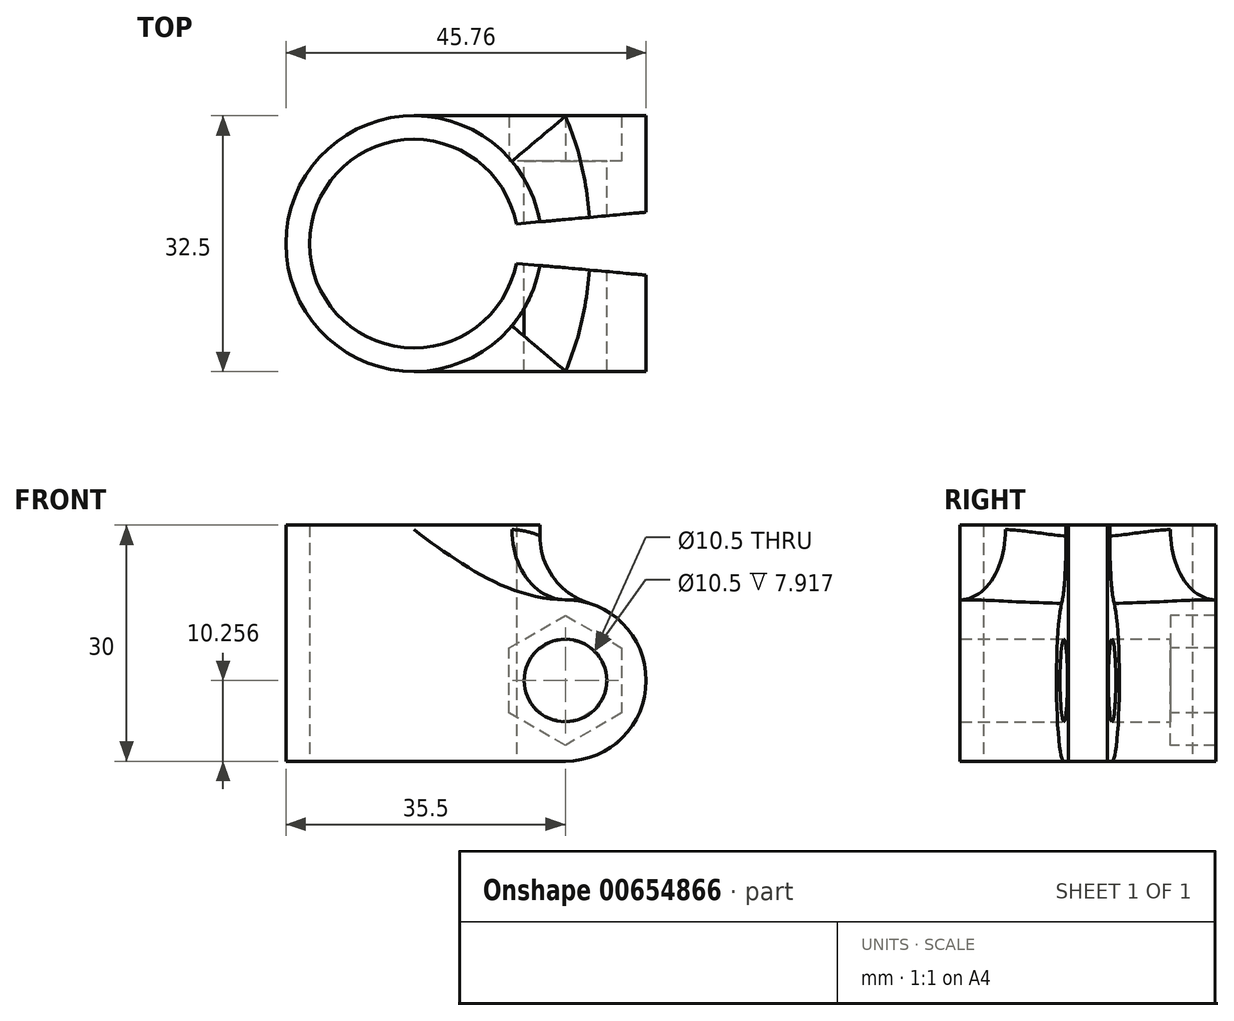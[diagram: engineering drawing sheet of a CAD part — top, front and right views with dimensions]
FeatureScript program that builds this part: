
annotation { "Feature Type Name" : "Feature", "Feature Type Description" : "" }
export const myFeature = defineFeature(function(context is Context, id is Id, definition is map)
    precondition{}
    {
        {
            var Q0;
            Q0=qCreatedBy(makeId("Top.planeOp"),FACE);
            var sketch = newSketch(context, id + "F0", { "sketchPlane" : qUnion([Q0])});
            skCircle(sketch, "E0", {"center": v(0, 0) * mm, "radius": 13.25 * mm});
            skCircle(sketch, "E1.0", {"center": v(0, 0) * mm, "radius": 16.25 * mm});
            skPoint(sketch, "E2", {"position": v(16.25, 0) * mm});
            skLineSegment(sketch, "E3.bottom", {"start": v(13.01, 2.5) * mm, "end": v(50, 2.5) * mm});
            skLineSegment(sketch, "E3.top", {"start": v(13.01, -2.5) * mm, "end": v(50, -2.5) * mm});
            skLineSegment(sketch, "E3.right", {"start": v(50, 2.5) * mm, "end": v(50, -2.5) * mm});
            skPoint(sketch, "E3.middle", {"position": v(27.77, 0) * mm});
            skPoint(sketch, "E3.left.end.orphan", {"position": v(5.53, -2.5) * mm});
            skPoint(sketch, "E4.orphan", {"position": v(5.53, 2.5) * mm});
            skSolve(sketch);
        }
        {
            var Q0;
            Q0=makeQuery(id+"F0.imprint","IMPRINT",FACE,{"disambiguationData":[TD([[makeQuery(id+"F0.imprint","IMPRINT",EDGE,{"derivedFrom":sQuery(id+"F0.wireOp",EDGE,"E0")}),-1.0]])]});
            var Q1;
            Q1=makeQuery(id+"F0.imprint","IMPRINT",FACE,{"disambiguationData":[TD([[makeQuery(id+"F0.imprint","IMPRINT",EDGE,{"derivedFrom":sQuery(id+"F0.wireOp",EDGE,"E0")}),1.0]])]});
            extrude(context, id + "F1", {"entities" : qUnion([Q0, Q1]), "depth" : 30 * mm, "offsetDistance" : 25 * mm});
        }
        {
            var Q0;
            Q0=qCreatedBy(makeId("Front.planeOp"),FACE);
            var sketch = newSketch(context, id + "F2", { "sketchPlane" : qUnion([Q0])});
            skCircle(sketch, "E5", {"center": v(19.25, 10.26) * mm, "radius": 5.25 * mm});
            skLineSegment(sketch, "E6", {"start": v(16.25, 0) * mm, "end": v(16.25, 30) * mm});
            skCircle(sketch, "E7.cCircle", {"center": v(19.25, 10.26) * mm, "radius": 7.15 * mm, "construction": true});
            skLineSegment(sketch, "E7.0", {"start": v(26.4, 14.38) * mm, "end": v(26.4, 6.13) * mm});
            skLineSegment(sketch, "E7.1", {"start": v(26.4, 6.13) * mm, "end": v(19.25, 2) * mm});
            skLineSegment(sketch, "E7.2", {"start": v(19.25, 2) * mm, "end": v(12.1, 6.13) * mm});
            skLineSegment(sketch, "E7.3", {"start": v(12.1, 6.13) * mm, "end": v(12.1, 14.38) * mm});
            skLineSegment(sketch, "E7.4", {"start": v(12.1, 14.38) * mm, "end": v(19.25, 18.51) * mm});
            skLineSegment(sketch, "E7.5", {"start": v(19.25, 18.51) * mm, "end": v(26.4, 14.38) * mm});
            skPoint(sketch, "E7.0.midPoint", {"position": v(26.4, 10.26) * mm});
            skLineSegment(sketch, "E8.bottom", {"start": v(19.25, 0) * mm, "end": v(0, 0) * mm});
            skLineSegment(sketch, "E8.top", {"start": v(19.25, 20.51) * mm, "end": v(0, 20.51) * mm});
            skLineSegment(sketch, "E8.left", {"start": v(19.25, 0) * mm, "end": v(19.25, 20.51) * mm, "construction": true});
            skLineSegment(sketch, "E8.right", {"start": v(0, 0) * mm, "end": v(0, 20.51) * mm});
            skArc(sketch, "E9", {"start": v(19.25, 20.51) * mm, "mid": v(9, 10.26) * mm, "end": v(19.25, 0) * mm, "construction": true});
            skArc(sketch, "E10", {"start": v(19.25, 0) * mm, "mid": v(29.5, 10.26) * mm, "end": v(19.25, 20.51) * mm});
            skSolve(sketch);
        }
        {
            var Q0;
            {var subQ0=sQuery(id+"F2.wireOp",EDGE,"E7.3");Q0=makeQuery(id+"F2.imprint","IMPRINT",FACE,{"disambiguationData":[TD([[makeQuery(id+"F2.imprint","IMPRINT",EDGE,{"derivedFrom":subQ0}),1.0]])]});}
            var Q1;
            Q1=makeQuery(id+"F2.imprint","IMPRINT",FACE,{"disambiguationData":[TD([[makeQuery(id+"F2.imprint","IMPRINT",EDGE,{"derivedFrom":sQuery(id+"F2.wireOp",EDGE,"E7.0")}),1.0]])]});
            var Q2;
            {var subQ1=sQuery(id+"F2.wireOp",EDGE,"E5");Q2=makeQuery(id+"F2.imprint","IMPRINT",FACE,{"disambiguationData":[TD([[makeQuery(id+"F2.imprint","IMPRINT",EDGE,{"derivedFrom":subQ1}),-1.0]])]});}
            var Q3;
            {var subQ0=sQuery(id+"F2.wireOp",EDGE,"E7.3");Q3=makeQuery(id+"F2.imprint","IMPRINT",FACE,{"disambiguationData":[TD([[makeQuery(id+"F2.imprint","IMPRINT",EDGE,{"derivedFrom":subQ0}),-1.0]])]});}
            var Q4;
            Q4=makeQuery(id+"F2.imprint","IMPRINT",FACE,{"disambiguationData":[TD([[makeQuery(id+"F2.imprint","IMPRINT",EDGE,{"derivedFrom":sQuery(id+"F2.wireOp",EDGE,"E7.0")}),-1.0]])]});
            extrude(context, id + "F3", {"entities" : qUnion([Q0, Q1, Q2, Q3, Q4]), "operationType" : NewBodyOperationType.ADD, "endBound" : BoundingType.SYMMETRIC, "depth" : 32.5 * mm, "offsetDistance" : 25 * mm});
        }
        {
            var Q0;
            {var subQ0=sQuery(id+"F2.wireOp",EDGE,"E7.3");Q0=makeQuery(id+"F2.imprint","IMPRINT",FACE,{"disambiguationData":[TD([[makeQuery(id+"F2.imprint","IMPRINT",EDGE,{"derivedFrom":subQ0}),-1.0]])]});}
            var Q1;
            {var subQ1=sQuery(id+"F2.wireOp",EDGE,"E5");Q1=makeQuery(id+"F2.imprint","IMPRINT",FACE,{"disambiguationData":[TD([[makeQuery(id+"F2.imprint","IMPRINT",EDGE,{"derivedFrom":subQ1}),-1.0]])]});}
            var Q2;
            Q2=makeQuery(id+"F2.imprint","IMPRINT",FACE,{"disambiguationData":[TD([[makeQuery(id+"F2.imprint","IMPRINT",EDGE,{"derivedFrom":sQuery(id+"F2.wireOp",EDGE,"E7.0")}),-1.0]])]});
            extrude(context, id + "F4", {"entities" : qUnion([Q0, Q1, Q2]), "operationType" : NewBodyOperationType.REMOVE, "oppositeDirection" : true, "depth" : (33 / 2) * mm, "offsetDistance" : 25 * mm, "hasSecondDirection" : true, "secondDirectionOppositeDirection" : true, "secondDirectionDepth" : 10.5 * mm});
        }
        {
            var Q0;
            Q0=makeQuery(id+"F3.boolean.opBoolean","INTERSECT",EDGE,{"derivedFrom":[makeQuery(id+"F1.opExtrude","SWEPT_FACE",FACE,{"disambiguationData":[OSD([sQuery(id+"F0.wireOp",EDGE,"E1.0")])]}),makeQuery(id+"F3.opExtrude","SWEPT_FACE",FACE,{"disambiguationData":[OSD([sQuery(id+"F2.wireOp",EDGE,"E8.top")])]})]});
            fillet(context, id + "F5", {"entities" : qUnion([Q0]), "radius" : 8.9 * mm, "tangentPropagation" : true, "allowEdgeOverflow" : false});
        }
        {
            var Q0;
            {var subQ0=sQuery(id+"F0.wireOp",EDGE,"E0");var subQ1=makeQuery(id+"F0.imprint","INTERSECT",VERTEX,{"derivedFrom":[subQ0,sQuery(id+"F0.wireOp",EDGE,"E3.bottom")]});Q0=makeQuery(id+"F0.imprint","IMPRINT",FACE,{"disambiguationData":[TD([[makeQuery(id+"F0.imprint","IMPRINT",EDGE,{"disambiguationData":[TD([[subQ1,-1.0]])],"derivedFrom":subQ0}),1.0]])]});}
            var Q1;
            {var subQ0=sQuery(id+"F0.wireOp",EDGE,"E3.bottom");var subQ1=sQuery(id+"F0.wireOp",EDGE,"E0");var subQ2=makeQuery(id+"F0.imprint","INTERSECT",VERTEX,{"derivedFrom":[subQ1,subQ0]});Q1=makeQuery(id+"F0.imprint","IMPRINT",FACE,{"disambiguationData":[TD([[makeQuery(id+"F0.imprint","IMPRINT",EDGE,{"disambiguationData":[TD([[subQ2,1.0]])],"derivedFrom":subQ1}),-1.0]])]});}
            var Q2;
            {var subQ5=sQuery(id+"F0.wireOp",EDGE,"E3.right");Q2=makeQuery(id+"F0.imprint","IMPRINT",FACE,{"disambiguationData":[TD([[makeQuery(id+"F0.imprint","IMPRINT",EDGE,{"derivedFrom":subQ5}),-1.0]])]});}
            extrude(context, id + "F6", {"entities" : qUnion([Q0, Q1, Q2]), "operationType" : NewBodyOperationType.REMOVE, "endBound" : BoundingType.THROUGH_ALL, "depth" : 25 * mm, "offsetDistance" : 25 * mm});
        }
        {
            var Q0;
            Q0=qCreatedBy(makeId("Top.planeOp"),FACE);
            var sketch = newSketch(context, id + "F7", { "sketchPlane" : qUnion([Q0])});
            skPoint(sketch, "E11.0", {"position": v(13.01, 2.5) * mm});
            skPoint(sketch, "E12.0", {"position": v(13.01, -2.5) * mm});
            skLineSegment(sketch, "E13", {"start": v(29.5, 16.25) * mm, "end": v(29.5, 2.5) * mm});
            skLineSegment(sketch, "E14", {"start": v(29.5, -2.5) * mm, "end": v(29.5, -16.25) * mm});
            skLineSegment(sketch, "E15", {"start": v(13.01, 2.5) * mm, "end": v(29.5, 4) * mm});
            skLineSegment(sketch, "E16.MirrorCS", {"start": v(13.01, -2.5) * mm, "end": v(29.5, -4) * mm});
            skLineSegment(sketch, "E17", {"start": v(13.01, -2.5) * mm, "end": v(13.01, 2.5) * mm});
            skLineSegment(sketch, "E18", {"start": v(29.5, 4) * mm, "end": v(29.5, -4) * mm});
            skSolve(sketch);
        }
        {
            var Q0;
            {var subQ0=sQuery(id+"F7.wireOp",EDGE,"E15");Q0=makeQuery(id+"F7.imprint","IMPRINT",FACE,{"disambiguationData":[TD([[makeQuery(id+"F7.imprint","IMPRINT",EDGE,{"derivedFrom":subQ0}),-1.0]])]});}
            extrude(context, id + "F8", {"entities" : qUnion([Q0]), "operationType" : NewBodyOperationType.REMOVE, "endBound" : BoundingType.THROUGH_ALL, "depth" : 25 * mm, "offsetDistance" : 25 * mm});
        }
        {
            var Q0;
            {var subQ0=sQuery(id+"F2.wireOp",EDGE,"E6");var subQ1=sQuery(id+"F2.wireOp",EDGE,"E5");var subQ2=makeQuery(id+"F2.imprint","INTERSECT",VERTEX,{"disambiguationData":[OD(0.0)],"derivedFrom":[subQ1,subQ0]});Q0=makeQuery(id+"F2.imprint","IMPRINT",FACE,{"disambiguationData":[TD([[makeQuery(id+"F2.imprint","IMPRINT",EDGE,{"disambiguationData":[TD([[subQ2,-1.0]])],"derivedFrom":subQ1}),1.0]])]});}
            var Q1;
            {var subQ0=sQuery(id+"F2.wireOp",EDGE,"E6");var subQ1=sQuery(id+"F2.wireOp",EDGE,"E5");var subQ2=makeQuery(id+"F2.imprint","INTERSECT",VERTEX,{"disambiguationData":[OD(0.0)],"derivedFrom":[subQ1,subQ0]});Q1=makeQuery(id+"F2.imprint","IMPRINT",FACE,{"disambiguationData":[TD([[makeQuery(id+"F2.imprint","IMPRINT",EDGE,{"disambiguationData":[TD([[subQ2,1.0]])],"derivedFrom":subQ1}),1.0]])]});}
            extrude(context, id + "F9", {"entities" : qUnion([Q0, Q1]), "operationType" : NewBodyOperationType.REMOVE, "endBound" : BoundingType.SYMMETRIC, "oppositeDirection" : true, "depth" : 25 * mm, "offsetDistance" : 25 * mm});
        }
    });
